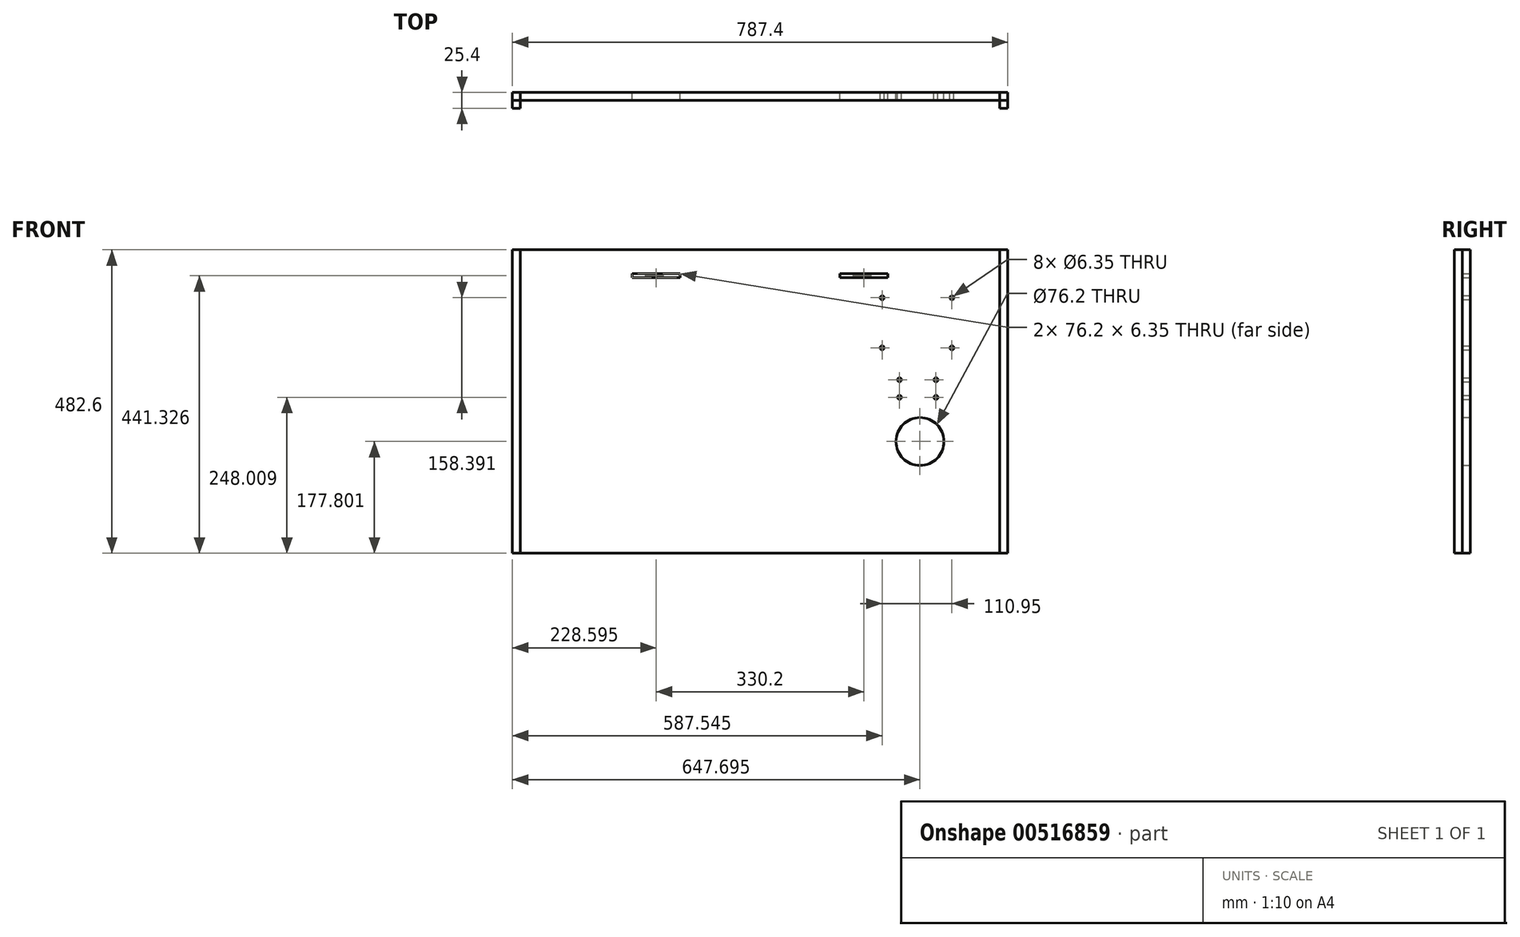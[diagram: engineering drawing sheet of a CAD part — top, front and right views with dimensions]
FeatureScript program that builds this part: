
annotation { "Feature Type Name" : "Feature", "Feature Type Description" : "" }
export const myFeature = defineFeature(function(context is Context, id is Id, definition is map)
    precondition{}
    {
        {
            var Q0;
            Q0=qCreatedBy(makeId("Front.planeOp"),FACE);
            var sketch = newSketch(context, id + "F0", { "sketchPlane" : qUnion([Q0])});
            skLineSegment(sketch, "E0.bottom", {"start": v(-296.05, 326.92) * mm, "end": v(491.35, 326.92) * mm});
            skLineSegment(sketch, "E0.top", {"start": v(-296.05, -155.68) * mm, "end": v(491.35, -155.68) * mm});
            skLineSegment(sketch, "E0.left", {"start": v(-296.05, 326.92) * mm, "end": v(-296.05, -155.68) * mm});
            skLineSegment(sketch, "E0.right", {"start": v(491.35, 326.92) * mm, "end": v(491.35, -155.68) * mm});
            skLineSegment(sketch, "E1", {"start": v(-283.35, 326.92) * mm, "end": v(-283.35, -155.68) * mm});
            skLineSegment(sketch, "E2", {"start": v(478.65, 326.92) * mm, "end": v(478.65, -155.68) * mm});
            skLineSegment(sketch, "E3.bottom", {"start": v(-105.55, 288.82) * mm, "end": v(-29.35, 288.82) * mm});
            skLineSegment(sketch, "E3.top", {"start": v(-105.55, 282.47) * mm, "end": v(-29.35, 282.47) * mm});
            skLineSegment(sketch, "E3.left", {"start": v(-105.55, 288.82) * mm, "end": v(-105.55, 282.47) * mm});
            skLineSegment(sketch, "E3.right", {"start": v(-29.35, 288.82) * mm, "end": v(-29.35, 282.47) * mm});
            skLineSegment(sketch, "E4.bottom", {"start": v(224.65, 288.82) * mm, "end": v(300.85, 288.82) * mm});
            skLineSegment(sketch, "E4.top", {"start": v(224.65, 282.47) * mm, "end": v(300.85, 282.47) * mm});
            skLineSegment(sketch, "E4.left", {"start": v(224.65, 288.82) * mm, "end": v(224.65, 282.47) * mm});
            skLineSegment(sketch, "E4.right", {"start": v(300.85, 288.82) * mm, "end": v(300.85, 282.47) * mm});
            skCircle(sketch, "E5", {"center": v(291.5, 250.72) * mm, "radius": 3.18 * mm});
            skCircle(sketch, "E6", {"center": v(402.45, 250.72) * mm, "radius": 3.18 * mm});
            skCircle(sketch, "E7", {"center": v(291.5, 171.05) * mm, "radius": 3.18 * mm});
            skCircle(sketch, "E8", {"center": v(402.45, 171.05) * mm, "radius": 3.18 * mm});
            skCircle(sketch, "E9", {"center": v(319.05, 120.25) * mm, "radius": 3.18 * mm});
            skCircle(sketch, "E10", {"center": v(377.05, 120.25) * mm, "radius": 3.18 * mm});
            skCircle(sketch, "E11", {"center": v(319.05, 92.33) * mm, "radius": 3.18 * mm});
            skCircle(sketch, "E12", {"center": v(377.05, 92.33) * mm, "radius": 3.18 * mm});
            skCircle(sketch, "E13", {"center": v(351.65, 22.12) * mm, "radius": 38.1 * mm});
            skSolve(sketch);
        }
        {
            var Q0;
            {var subQ0=sQuery(id+"F0.wireOp",EDGE,"E0.left");Q0=makeQuery(id+"F0.imprint","IMPRINT",FACE,{"disambiguationData":[TD([[makeQuery(id+"F0.imprint","IMPRINT",EDGE,{"derivedFrom":subQ0}),1.0]])]});}
            var Q1;
            {var subQ0=sQuery(id+"F0.wireOp",EDGE,"E0.right");Q1=makeQuery(id+"F0.imprint","IMPRINT",FACE,{"disambiguationData":[TD([[makeQuery(id+"F0.imprint","IMPRINT",EDGE,{"derivedFrom":subQ0}),-1.0]])]});}
            extrude(context, id + "F1", {"entities" : qUnion([Q0, Q1]), "depth" : 25.4 * mm, "offsetDistance" : 25.4 * mm});
        }
        {
            var Q0;
            Q0 = qSketchRegion(id + "F0", true);
            extrude(context, id + "F2", {"entities" : qUnion([Q0]), "depth" : 12.7 * mm, "offsetDistance" : 25.4 * mm});
        }
    });
